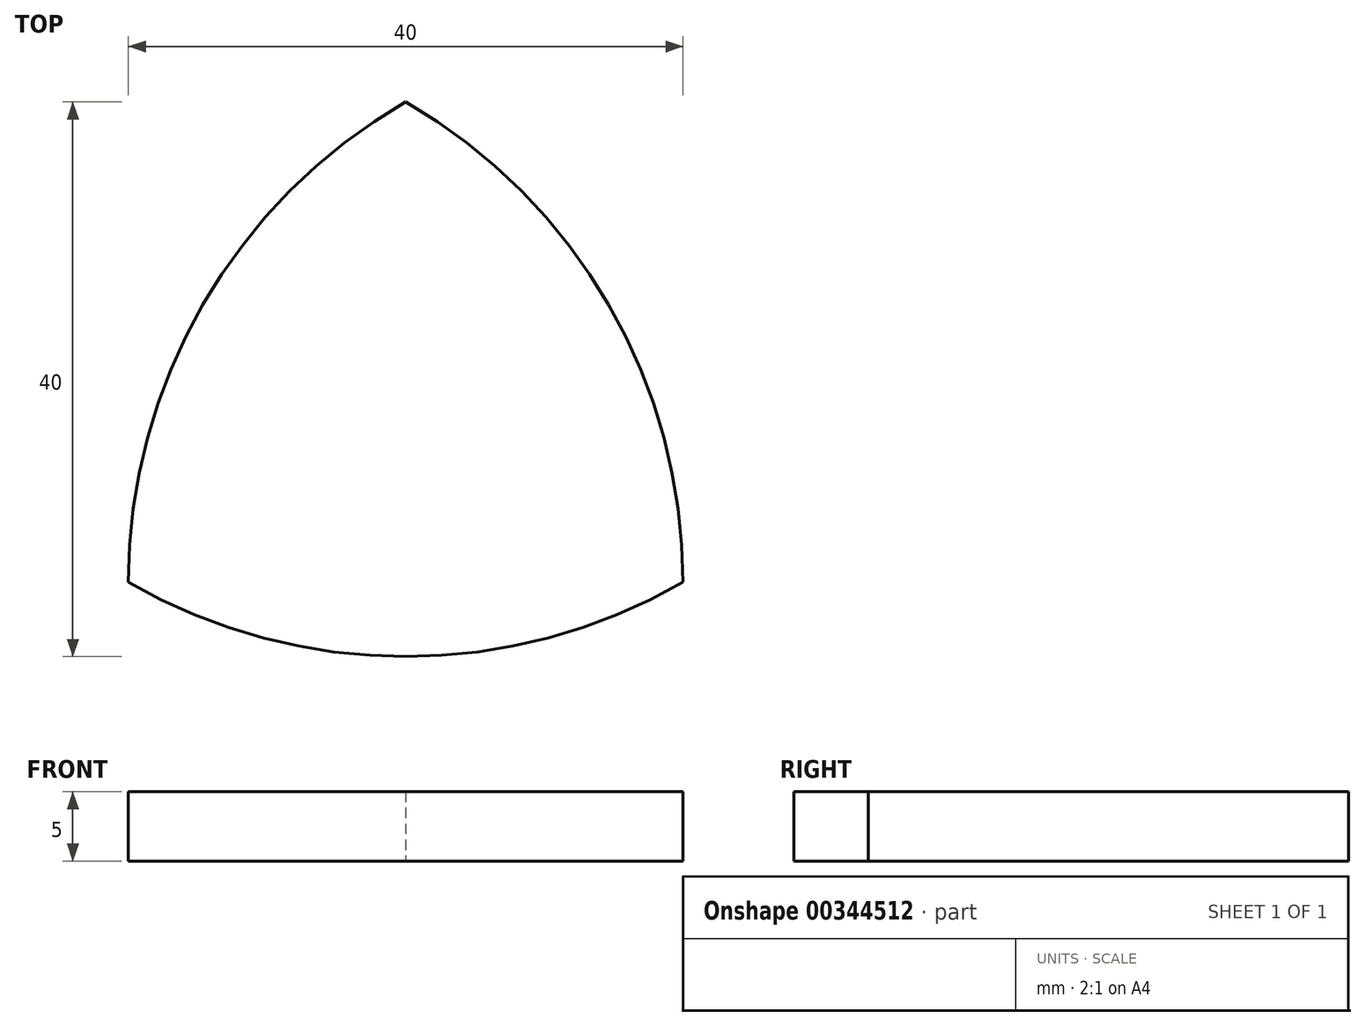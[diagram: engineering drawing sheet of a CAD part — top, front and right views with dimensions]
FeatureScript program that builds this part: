
annotation { "Feature Type Name" : "Feature", "Feature Type Description" : "" }
export const myFeature = defineFeature(function(context is Context, id is Id, definition is map)
    precondition{}
    {
        {
            var Q0;
            Q0=qCreatedBy(makeId("Top.planeOp"),FACE);
            var sketch = newSketch(context, id + "F0", { "sketchPlane" : qUnion([Q0])});
            skLineSegment(sketch, "E0", {"start": v(-20, 0) * mm, "end": v(0, 34.64) * mm});
            skLineSegment(sketch, "E1", {"start": v(0, 34.64) * mm, "end": v(20, 0) * mm});
            skLineSegment(sketch, "E2", {"start": v(20, 0) * mm, "end": v(-20, 0) * mm});
            skArc(sketch, "E3", {"start": v(20, 0) * mm, "mid": v(14.64, 20) * mm, "end": v(0, 34.64) * mm});
            skArc(sketch, "E4", {"start": v(0, 34.64) * mm, "mid": v(-14.64, 20) * mm, "end": v(-20, 0) * mm});
            skArc(sketch, "E5", {"start": v(-20, 0) * mm, "mid": v(0, -5.36) * mm, "end": v(20, 0) * mm});
            skSolve(sketch);
        }
        {
            var Q0;
            Q0 = qSketchRegion(id + "F0", true);
            extrude(context, id + "F1", {"entities" : qUnion([Q0]), "depth" : 5 * mm});
        }
    });
